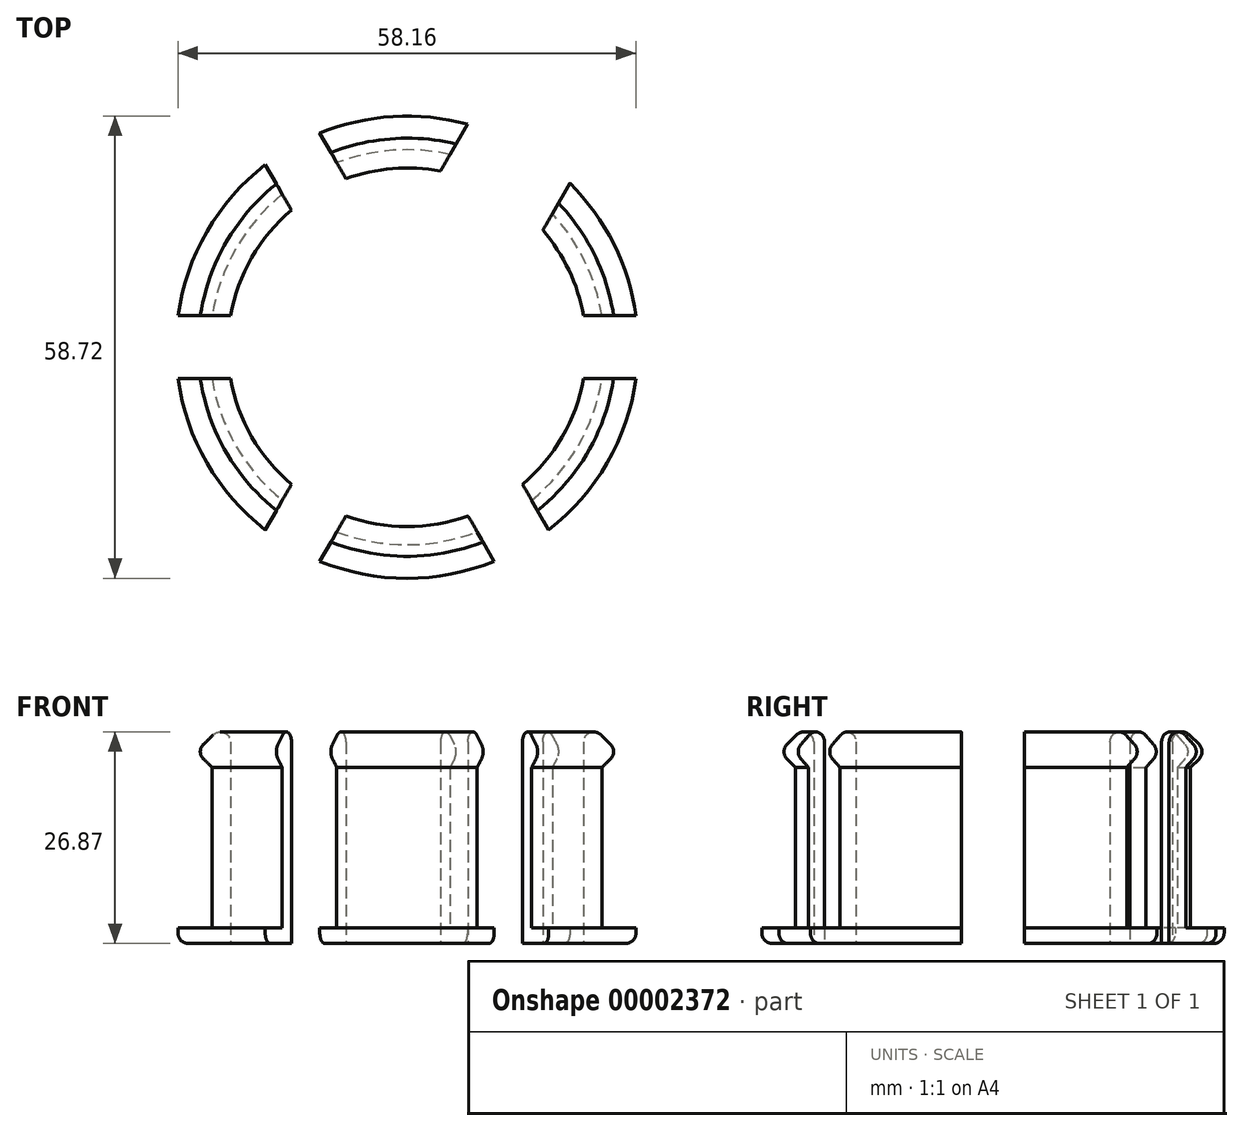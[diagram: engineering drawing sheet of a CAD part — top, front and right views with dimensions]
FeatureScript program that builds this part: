
annotation { "Feature Type Name" : "Feature", "Feature Type Description" : "" }
export const myFeature = defineFeature(function(context is Context, id is Id, definition is map)
    precondition{}
    {
        {
            var Q0;
            Q0=qCreatedBy(makeId("Top.planeOp"),FACE);
            var sketch = newSketch(context, id + "F0", { "sketchPlane" : qUnion([Q0])});
            skArc(sketch, "E0", {"start": v(25.08, 4) * mm, "mid": v(22.84, 11.11) * mm, "end": v(18.63, 17.27) * mm});
            skArc(sketch, "E1.0", {"start": v(29.08, 4) * mm, "mid": v(26.27, 13.1) * mm, "end": v(20.69, 20.83) * mm});
            skLineSegment(sketch, "E2.bottom", {"start": v(21.4, -4) * mm, "end": v(29.08, -4) * mm});
            skLineSegment(sketch, "E2.top", {"start": v(21.4, 4) * mm, "end": v(29.08, 4) * mm});
            skArc(sketch, "E3", {"start": v(21.4, 4) * mm, "mid": v(17.4, 0) * mm, "end": v(21.4, -4) * mm});
            skArc(sketch, "E4.0", {"start": v(22.77, 4) * mm, "mid": v(20.87, 9.96) * mm, "end": v(17.43, 15.2) * mm});
            skLineSegment(sketch, "E5.1.0", {"start": v(7.24, -20.53) * mm, "end": v(11.08, -27.19) * mm});
            skLineSegment(sketch, "E5.1.1", {"start": v(14.16, -16.53) * mm, "end": v(18, -23.19) * mm});
            skArc(sketch, "E5.1.2", {"start": v(14.16, -16.53) * mm, "mid": v(8.7, -15.07) * mm, "end": v(7.24, -20.53) * mm});
            skLineSegment(sketch, "E5.2.0", {"start": v(-14.16, -16.53) * mm, "end": v(-18, -23.19) * mm});
            skLineSegment(sketch, "E5.2.1", {"start": v(-7.24, -20.53) * mm, "end": v(-11.08, -27.19) * mm});
            skArc(sketch, "E5.2.2", {"start": v(-7.24, -20.53) * mm, "mid": v(-8.7, -15.07) * mm, "end": v(-14.16, -16.53) * mm});
            skLineSegment(sketch, "E5.3.0", {"start": v(-21.4, 4) * mm, "end": v(-29.08, 4) * mm});
            skLineSegment(sketch, "E5.3.1", {"start": v(-21.4, -4) * mm, "end": v(-29.08, -4) * mm});
            skArc(sketch, "E5.3.2", {"start": v(-21.4, -4) * mm, "mid": v(-17.4, 0) * mm, "end": v(-21.4, 4) * mm});
            skLineSegment(sketch, "E5.4.0", {"start": v(-7.24, 20.53) * mm, "end": v(-11.08, 27.19) * mm});
            skLineSegment(sketch, "E5.4.1", {"start": v(-14.16, 16.53) * mm, "end": v(-18, 23.19) * mm});
            skArc(sketch, "E5.4.2", {"start": v(-14.16, 16.53) * mm, "mid": v(-8.7, 15.07) * mm, "end": v(-7.24, 20.53) * mm});
            skLineSegment(sketch, "E5.anchor1", {"start": v(0, 0) * mm, "end": v(21.4, 0) * mm, "construction": true});
            skLineSegment(sketch, "E5.anchor2", {"start": v(0, 0) * mm, "end": v(-10.7, 18.53) * mm, "construction": true});
            skArc(sketch, "E6.trimOffspring", {"start": v(-14.85, 17.72) * mm, "mid": v(-20.02, 11.56) * mm, "end": v(-22.77, 4) * mm});
            skArc(sketch, "E7.trimOffspring", {"start": v(-16, 19.72) * mm, "mid": v(-22, 12.7) * mm, "end": v(-25.08, 4) * mm});
            skArc(sketch, "E8.trimOffspring", {"start": v(-18, 23.19) * mm, "mid": v(-25.42, 14.68) * mm, "end": v(-29.08, 4) * mm});
            skArc(sketch, "E9.trimOffspring", {"start": v(-29.08, -4) * mm, "mid": v(-25.42, -14.68) * mm, "end": v(-18, -23.19) * mm});
            skArc(sketch, "E10.trimOffspring", {"start": v(-25.08, -4) * mm, "mid": v(-22, -12.7) * mm, "end": v(-16, -19.72) * mm});
            skArc(sketch, "E11.trimOffspring", {"start": v(-22.77, -4) * mm, "mid": v(-20.02, -11.56) * mm, "end": v(-14.85, -17.72) * mm});
            skArc(sketch, "E12.trimOffspring", {"start": v(-7.92, -21.72) * mm, "mid": v(0, -23.12) * mm, "end": v(7.92, -21.72) * mm});
            skArc(sketch, "E13.trimOffspring", {"start": v(-9.08, -23.72) * mm, "mid": v(0, -25.4) * mm, "end": v(9.08, -23.72) * mm});
            skArc(sketch, "E14.trimOffspring", {"start": v(-11.08, -27.19) * mm, "mid": v(0, -29.36) * mm, "end": v(11.08, -27.19) * mm});
            skArc(sketch, "E15.trimOffspring", {"start": v(14.85, -17.72) * mm, "mid": v(20.02, -11.56) * mm, "end": v(22.77, -4) * mm});
            skArc(sketch, "E16.trimOffspring", {"start": v(16, -19.72) * mm, "mid": v(22, -12.7) * mm, "end": v(25.08, -4) * mm});
            skArc(sketch, "E17.trimOffspring", {"start": v(18, -23.19) * mm, "mid": v(25.42, -14.68) * mm, "end": v(29.08, -4) * mm});
            skLineSegment(sketch, "E18.1.0", {"start": v(15.45, 11.75) * mm, "end": v(20.69, 20.83) * mm});
            skLineSegment(sketch, "E18.1.1", {"start": v(2.45, 19.25) * mm, "end": v(7.7, 28.33) * mm});
            skArc(sketch, "E18.1.2", {"start": v(2.45, 19.25) * mm, "mid": v(5.2, 9) * mm, "end": v(15.45, 11.75) * mm});
            skLineSegment(sketch, "E18.anchor2", {"start": v(0, 0) * mm, "end": v(8.95, 15.5) * mm, "construction": true});
            skArc(sketch, "E19.trimOffspring", {"start": v(4.44, 22.7) * mm, "mid": v(-1.8, 23.05) * mm, "end": v(-7.92, 21.72) * mm});
            skArc(sketch, "E20.trimOffspring", {"start": v(5.64, 24.77) * mm, "mid": v(-1.8, 25.34) * mm, "end": v(-9.08, 23.72) * mm});
            skArc(sketch, "E21.trimOffspring", {"start": v(7.7, 28.33) * mm, "mid": v(-1.78, 29.3) * mm, "end": v(-11.08, 27.19) * mm});
            skLineSegment(sketch, "E22", {"start": v(-14.16, -16.53) * mm, "end": v(-16, -19.72) * mm});
            skLineSegment(sketch, "E23", {"start": v(4.44, 22.7) * mm, "end": v(5.64, 24.77) * mm});
            skLineSegment(sketch, "E24", {"start": v(-14.85, 17.72) * mm, "end": v(-18, 23.19) * mm});
            skLineSegment(sketch, "E25", {"start": v(-11.08, 27.19) * mm, "end": v(-7.92, 21.72) * mm});
            skLineSegment(sketch, "E26", {"start": v(7.7, 28.33) * mm, "end": v(4.44, 22.7) * mm});
            skLineSegment(sketch, "E27", {"start": v(20.69, 20.83) * mm, "end": v(17.43, 15.2) * mm});
            skLineSegment(sketch, "E28", {"start": v(29.08, 4) * mm, "end": v(22.77, 4) * mm});
            skLineSegment(sketch, "E29", {"start": v(29.08, -4) * mm, "end": v(22.77, -4) * mm});
            skLineSegment(sketch, "E30", {"start": v(18, -23.19) * mm, "end": v(14.85, -17.72) * mm});
            skLineSegment(sketch, "E31", {"start": v(-11.08, -27.19) * mm, "end": v(-7.92, -21.72) * mm});
            skLineSegment(sketch, "E32", {"start": v(-18, -23.19) * mm, "end": v(-14.85, -17.72) * mm});
            skLineSegment(sketch, "E33", {"start": v(-29.08, -4) * mm, "end": v(-22.77, -4) * mm});
            skLineSegment(sketch, "E34", {"start": v(-29.08, 4) * mm, "end": v(-22.77, 4) * mm});
            skLineSegment(sketch, "E35", {"start": v(7.92, -21.72) * mm, "end": v(11.08, -27.19) * mm});
            skLineSegment(sketch, "E36", {"start": v(29.08, -4) * mm, "end": v(29.08, 4) * mm});
            skLineSegment(sketch, "E37", {"start": v(-18, 23.19) * mm, "end": v(-11.08, 27.19) * mm});
            skLineSegment(sketch, "E38", {"start": v(-29.08, -4) * mm, "end": v(-29.08, 4) * mm});
            skLineSegment(sketch, "E39", {"start": v(-18, -23.19) * mm, "end": v(-11.08, -27.19) * mm});
            skLineSegment(sketch, "E40", {"start": v(11.08, -27.19) * mm, "end": v(18, -23.19) * mm});
            skLineSegment(sketch, "E41", {"start": v(7.7, 28.33) * mm, "end": v(20.69, 20.83) * mm});
            skSolve(sketch);
        }
        {
            var Q0;
            {var subQ2=sQuery(id+"F0.wireOp",EDGE,"E0");Q0=makeQuery(id+"F0.imprint","IMPRINT",FACE,{"disambiguationData":[TD([[makeQuery(id+"F0.imprint","IMPRINT",EDGE,{"derivedFrom":subQ2}),-1.0]])]});}
            var Q1;
            {var subQ2=sQuery(id+"F0.wireOp",EDGE,"E7.trimOffspring");Q1=makeQuery(id+"F0.imprint","IMPRINT",FACE,{"disambiguationData":[TD([[makeQuery(id+"F0.imprint","IMPRINT",EDGE,{"derivedFrom":subQ2}),-1.0]])]});}
            var Q2;
            {var subQ2=sQuery(id+"F0.wireOp",EDGE,"E9.trimOffspring");Q2=makeQuery(id+"F0.imprint","IMPRINT",FACE,{"disambiguationData":[TD([[makeQuery(id+"F0.imprint","IMPRINT",EDGE,{"derivedFrom":subQ2}),1.0]])]});}
            var Q3;
            {var subQ2=sQuery(id+"F0.wireOp",EDGE,"E13.trimOffspring");Q3=makeQuery(id+"F0.imprint","IMPRINT",FACE,{"disambiguationData":[TD([[makeQuery(id+"F0.imprint","IMPRINT",EDGE,{"derivedFrom":subQ2}),-1.0]])]});}
            var Q4;
            {var subQ2=sQuery(id+"F0.wireOp",EDGE,"E16.trimOffspring");Q4=makeQuery(id+"F0.imprint","IMPRINT",FACE,{"disambiguationData":[TD([[makeQuery(id+"F0.imprint","IMPRINT",EDGE,{"derivedFrom":subQ2}),-1.0]])]});}
            var Q5;
            {var subQ2=sQuery(id+"F0.wireOp",EDGE,"E20.trimOffspring");Q5=makeQuery(id+"F0.imprint","IMPRINT",FACE,{"disambiguationData":[TD([[makeQuery(id+"F0.imprint","IMPRINT",EDGE,{"derivedFrom":subQ2}),-1.0]])]});}
            var Q6;
            {var subQ2=sQuery(id+"F0.wireOp",EDGE,"E18.1.0");Q6=makeQuery(id+"F0.imprint","IMPRINT",FACE,{"disambiguationData":[TD([[makeQuery(id+"F0.imprint","IMPRINT",EDGE,{"derivedFrom":subQ2}),1.0]])]});}
            var Q7;
            {var subQ2=sQuery(id+"F0.wireOp",EDGE,"E12.trimOffspring");Q7=makeQuery(id+"F0.imprint","IMPRINT",FACE,{"disambiguationData":[TD([[makeQuery(id+"F0.imprint","IMPRINT",EDGE,{"derivedFrom":subQ2}),-1.0]])]});}
            var Q8;
            {var subQ2=sQuery(id+"F0.wireOp",EDGE,"E10.trimOffspring");Q8=makeQuery(id+"F0.imprint","IMPRINT",FACE,{"disambiguationData":[TD([[makeQuery(id+"F0.imprint","IMPRINT",EDGE,{"derivedFrom":subQ2}),1.0]])]});}
            var Q9;
            {var subQ2=sQuery(id+"F0.wireOp",EDGE,"E6.trimOffspring");Q9=makeQuery(id+"F0.imprint","IMPRINT",FACE,{"disambiguationData":[TD([[makeQuery(id+"F0.imprint","IMPRINT",EDGE,{"derivedFrom":subQ2}),-1.0]])]});}
            var Q10;
            Q10=makeQuery(id+"F0.imprint","IMPRINT",FACE,{"disambiguationData":[TD([[makeQuery(id+"F0.imprint","IMPRINT",EDGE,{"derivedFrom":sQuery(id+"F0.wireOp",EDGE,"E2.bottom")}),-1.0]])]});
            var Q11;
            {var subQ2=sQuery(id+"F0.wireOp",EDGE,"E15.trimOffspring");Q11=makeQuery(id+"F0.imprint","IMPRINT",FACE,{"disambiguationData":[TD([[makeQuery(id+"F0.imprint","IMPRINT",EDGE,{"derivedFrom":subQ2}),-1.0]])]});}
            var Q12;
            {var subQ2=sQuery(id+"F0.wireOp",EDGE,"E0");Q12=makeQuery(id+"F0.imprint","IMPRINT",FACE,{"disambiguationData":[TD([[makeQuery(id+"F0.imprint","IMPRINT",EDGE,{"derivedFrom":subQ2}),1.0]])]});}
            var Q13;
            {var subQ2=sQuery(id+"F0.wireOp",EDGE,"E19.trimOffspring");Q13=makeQuery(id+"F0.imprint","IMPRINT",FACE,{"disambiguationData":[TD([[makeQuery(id+"F0.imprint","IMPRINT",EDGE,{"derivedFrom":subQ2}),-1.0]])]});}
            var Q14;
            {var subQ3=sQuery(id+"F0.wireOp",EDGE,"E2.bottom");Q14=makeQuery(id+"F0.imprint","IMPRINT",FACE,{"disambiguationData":[TD([[makeQuery(id+"F0.imprint","IMPRINT",EDGE,{"derivedFrom":subQ3}),1.0]])]});}
            var Q15;
            {var subQ6=sQuery(id+"F0.wireOp",EDGE,"E5.1.0");Q15=makeQuery(id+"F0.imprint","IMPRINT",FACE,{"disambiguationData":[TD([[makeQuery(id+"F0.imprint","IMPRINT",EDGE,{"derivedFrom":subQ6}),1.0]])]});}
            var Q16;
            {var subQ6=sQuery(id+"F0.wireOp",EDGE,"E5.2.1");Q16=makeQuery(id+"F0.imprint","IMPRINT",FACE,{"disambiguationData":[TD([[makeQuery(id+"F0.imprint","IMPRINT",EDGE,{"derivedFrom":subQ6}),-1.0]])]});}
            var Q17;
            {var subQ2=sQuery(id+"F0.wireOp",EDGE,"E5.3.0");Q17=makeQuery(id+"F0.imprint","IMPRINT",FACE,{"disambiguationData":[TD([[makeQuery(id+"F0.imprint","IMPRINT",EDGE,{"derivedFrom":subQ2}),1.0]])]});}
            var Q18;
            {var subQ3=sQuery(id+"F0.wireOp",EDGE,"E5.4.0");Q18=makeQuery(id+"F0.imprint","IMPRINT",FACE,{"disambiguationData":[TD([[makeQuery(id+"F0.imprint","IMPRINT",EDGE,{"derivedFrom":subQ3}),1.0]])]});}
            extrude(context, id + "F1", {"entities" : qUnion([Q0, Q1, Q2, Q3, Q4, Q5, Q6, Q7, Q8, Q9, Q10, Q11, Q12, Q13, Q14, Q15, Q16, Q17, Q18]), "depth" : 2 * mm});
        }
        {
            var Q0;
            Q0=qCreatedBy(makeId("Front.planeOp"),FACE);
            var sketch = newSketch(context, id + "F2", { "sketchPlane" : qUnion([Q0])});
            skLineSegment(sketch, "E42", {"start": v(27.08, 24.35) * mm, "end": v(25.08, 22.35) * mm});
            skLineSegment(sketch, "E43", {"start": v(25.08, 22.35) * mm, "end": v(25.08, 26.35) * mm, "construction": true});
            skLineSegment(sketch, "E44", {"start": v(25.08, 24.35) * mm, "end": v(27.08, 24.35) * mm, "construction": true});
            skLineSegment(sketch, "E45", {"start": v(22.77, 28.66) * mm, "end": v(25.08, 26.35) * mm});
            skLineSegment(sketch, "E46", {"start": v(25.08, 26.35) * mm, "end": v(27.08, 24.35) * mm});
            skPoint(sketch, "E47.0", {"position": v(25.08, 0) * mm});
            skPoint(sketch, "E47.1", {"position": v(22.77, 0) * mm});
            skLineSegment(sketch, "E48", {"start": v(25.08, 22.35) * mm, "end": v(25.08, 0) * mm});
            skLineSegment(sketch, "E49", {"start": v(22.77, 0) * mm, "end": v(22.77, 28.66) * mm});
            skLineSegment(sketch, "E50", {"start": v(25.08, 0) * mm, "end": v(22.77, 0) * mm});
            skLineSegment(sketch, "E51", {"start": v(0, 0) * mm, "end": v(0, 28.66) * mm});
            skSolve(sketch);
        }
        {
            var Q0;
            Q0=makeQuery(id+"F2.imprint","IMPRINT",FACE,{"disambiguationData":[TD([[makeQuery(id+"F2.imprint","IMPRINT",EDGE,{"derivedFrom":sQuery(id+"F2.wireOp",EDGE,"E42")}),-1.0]])]});
            var Q1;
            Q1=sQuery(id+"F2.wireOp",EDGE,"E42");
            var Q2;
            Q2=sQuery(id+"F2.wireOp",EDGE,"E46");
            var Q3;
            Q3=sQuery(id+"F2.wireOp",EDGE,"E45");
            var Q4;
            Q4=sQuery(id+"F2.wireOp",EDGE,"E49");
            var Q5;
            Q5=sQuery(id+"F2.wireOp",EDGE,"E48");
            var Q6;
            Q6=sQuery(id+"F2.wireOp",EDGE,"E51");
            revolve(context, id + "F3", {"operationType" : NewBodyOperationType.ADD, "entities" : qUnion([Q0]), "surfaceEntities" : qUnion([Q1, Q2, Q3, Q4, Q5]), "axis" : qUnion([Q6]), "revolveType" : RevolveType.FULL});
        }
        {
            var Q0;
            {var subQ6=sQuery(id+"F0.wireOp",EDGE,"E5.2.1");Q0=makeQuery(id+"F0.imprint","IMPRINT",FACE,{"disambiguationData":[TD([[makeQuery(id+"F0.imprint","IMPRINT",EDGE,{"derivedFrom":subQ6}),-1.0]])]});}
            var Q1;
            {var subQ6=sQuery(id+"F0.wireOp",EDGE,"E5.1.0");Q1=makeQuery(id+"F0.imprint","IMPRINT",FACE,{"disambiguationData":[TD([[makeQuery(id+"F0.imprint","IMPRINT",EDGE,{"derivedFrom":subQ6}),1.0]])]});}
            var Q2;
            {var subQ3=sQuery(id+"F0.wireOp",EDGE,"E2.bottom");Q2=makeQuery(id+"F0.imprint","IMPRINT",FACE,{"disambiguationData":[TD([[makeQuery(id+"F0.imprint","IMPRINT",EDGE,{"derivedFrom":subQ3}),1.0]])]});}
            var Q3;
            {var subQ2=sQuery(id+"F0.wireOp",EDGE,"E18.1.0");Q3=makeQuery(id+"F0.imprint","IMPRINT",FACE,{"disambiguationData":[TD([[makeQuery(id+"F0.imprint","IMPRINT",EDGE,{"derivedFrom":subQ2}),1.0]])]});}
            var Q4;
            {var subQ3=sQuery(id+"F0.wireOp",EDGE,"E5.4.0");Q4=makeQuery(id+"F0.imprint","IMPRINT",FACE,{"disambiguationData":[TD([[makeQuery(id+"F0.imprint","IMPRINT",EDGE,{"derivedFrom":subQ3}),1.0]])]});}
            var Q5;
            {var subQ2=sQuery(id+"F0.wireOp",EDGE,"E5.3.0");Q5=makeQuery(id+"F0.imprint","IMPRINT",FACE,{"disambiguationData":[TD([[makeQuery(id+"F0.imprint","IMPRINT",EDGE,{"derivedFrom":subQ2}),1.0]])]});}
            extrude(context, id + "F4", {"entities" : qUnion([Q0, Q1, Q2, Q3, Q4, Q5]), "operationType" : NewBodyOperationType.REMOVE, "endBound" : BoundingType.THROUGH_ALL, "depth" : 31.75 * mm});
        }
        {
            var Q0;
            Q0=makeQuery(id+"F4.boolean.opBoolean","COPY",EDGE,{"derivedFrom":makeQuery(id+"F4.opExtrude","CAP_EDGE",EDGE,{"disambiguationData":[OSD([sQuery(id+"F0.wireOp",EDGE,"E5.2.2")])],"isStart":true})});
            var Q1;
            Q1=makeQuery(id+"F4.boolean.opBoolean","COPY",EDGE,{"derivedFrom":makeQuery(id+"F4.opExtrude","CAP_EDGE",EDGE,{"disambiguationData":[OSD([sQuery(id+"F0.wireOp",EDGE,"E5.1.2")])],"isStart":true})});
            var Q2;
            Q2=makeQuery(id+"F4.boolean.opBoolean","COPY",EDGE,{"derivedFrom":makeQuery(id+"F4.opExtrude","CAP_EDGE",EDGE,{"disambiguationData":[OSD([sQuery(id+"F0.wireOp",EDGE,"E3")])],"isStart":true})});
            var Q3;
            Q3=makeQuery(id+"F4.boolean.opBoolean","COPY",EDGE,{"derivedFrom":makeQuery(id+"F4.opExtrude","CAP_EDGE",EDGE,{"disambiguationData":[OSD([sQuery(id+"F0.wireOp",EDGE,"E18.1.2")])],"isStart":true})});
            var Q4;
            Q4=makeQuery(id+"F4.boolean.opBoolean","COPY",EDGE,{"derivedFrom":makeQuery(id+"F4.opExtrude","CAP_EDGE",EDGE,{"disambiguationData":[OSD([sQuery(id+"F0.wireOp",EDGE,"E5.4.2")])],"isStart":true})});
            var Q5;
            Q5=makeQuery(id+"F4.boolean.opBoolean","COPY",EDGE,{"derivedFrom":makeQuery(id+"F4.opExtrude","CAP_EDGE",EDGE,{"disambiguationData":[OSD([sQuery(id+"F0.wireOp",EDGE,"E5.3.2")])],"isStart":true})});
            var Q6;
            Q6=makeQuery(id+"F1.opExtrude","CAP_EDGE",EDGE,{"disambiguationData":[OSD([sQuery(id+"F0.wireOp",EDGE,"E21.trimOffspring")])],"isStart":true});
            var Q7;
            Q7=makeQuery(id+"F1.opExtrude","CAP_EDGE",EDGE,{"disambiguationData":[OSD([sQuery(id+"F0.wireOp",EDGE,"E8.trimOffspring")])],"isStart":true});
            var Q8;
            Q8=makeQuery(id+"F1.opExtrude","CAP_EDGE",EDGE,{"disambiguationData":[OSD([sQuery(id+"F0.wireOp",EDGE,"E9.trimOffspring")])],"isStart":true});
            var Q9;
            Q9=makeQuery(id+"F1.opExtrude","CAP_EDGE",EDGE,{"disambiguationData":[OSD([sQuery(id+"F0.wireOp",EDGE,"E14.trimOffspring")])],"isStart":true});
            var Q10;
            Q10=makeQuery(id+"F1.opExtrude","CAP_EDGE",EDGE,{"disambiguationData":[OSD([sQuery(id+"F0.wireOp",EDGE,"E17.trimOffspring")])],"isStart":true});
            var Q11;
            Q11=makeQuery(id+"F1.opExtrude","CAP_EDGE",EDGE,{"disambiguationData":[OSD([sQuery(id+"F0.wireOp",EDGE,"E1.0")])],"isStart":true});
            var Q12;
            {var subQ0=makeQuery(id+"F1.opExtrude","CAP_FACE",FACE,{"disambiguationData":[OSD([sQuery(id+"F0.wireOp",EDGE,"E1.0"),sQuery(id+"F0.wireOp",EDGE,"E8.trimOffspring"),sQuery(id+"F0.wireOp",EDGE,"E9.trimOffspring"),sQuery(id+"F0.wireOp",EDGE,"E14.trimOffspring"),sQuery(id+"F0.wireOp",EDGE,"E17.trimOffspring"),sQuery(id+"F0.wireOp",EDGE,"E21.trimOffspring"),sQuery(id+"F0.wireOp",EDGE,"E36"),sQuery(id+"F0.wireOp",EDGE,"E37"),sQuery(id+"F0.wireOp",EDGE,"E38"),sQuery(id+"F0.wireOp",EDGE,"E39"),sQuery(id+"F0.wireOp",EDGE,"E40"),sQuery(id+"F0.wireOp",EDGE,"E41")])],"isStart":false});var subQ1=makeQuery(id+"F3.opRevolve","SWEPT_FACE",FACE,{"disambiguationData":[OSD([sQuery(id+"F2.wireOp",EDGE,"E49")])]});Q12=makeQuery(id+"F4.boolean.opBoolean","SPLIT",EDGE,{"disambiguationData":[TD([makeQuery(id+"F4.opExtrude","SWEPT_FACE",FACE,{"disambiguationData":[OSD([sQuery(id+"F0.wireOp",EDGE,"E5.4.0"),sQuery(id+"F0.wireOp",EDGE,"E25")])]})])],"derivedFrom":makeQuery(id+"F3.boolean.opBoolean","INTERSECT",EDGE,{"derivedFrom":[subQ0,subQ1]})});}
            var Q13;
            {var subQ0=makeQuery(id+"F1.opExtrude","CAP_FACE",FACE,{"disambiguationData":[OSD([sQuery(id+"F0.wireOp",EDGE,"E1.0"),sQuery(id+"F0.wireOp",EDGE,"E8.trimOffspring"),sQuery(id+"F0.wireOp",EDGE,"E9.trimOffspring"),sQuery(id+"F0.wireOp",EDGE,"E14.trimOffspring"),sQuery(id+"F0.wireOp",EDGE,"E17.trimOffspring"),sQuery(id+"F0.wireOp",EDGE,"E21.trimOffspring"),sQuery(id+"F0.wireOp",EDGE,"E36"),sQuery(id+"F0.wireOp",EDGE,"E37"),sQuery(id+"F0.wireOp",EDGE,"E38"),sQuery(id+"F0.wireOp",EDGE,"E39"),sQuery(id+"F0.wireOp",EDGE,"E40"),sQuery(id+"F0.wireOp",EDGE,"E41")])],"isStart":false});var subQ1=makeQuery(id+"F3.opRevolve","SWEPT_FACE",FACE,{"disambiguationData":[OSD([sQuery(id+"F2.wireOp",EDGE,"E49")])]});Q13=makeQuery(id+"F4.boolean.opBoolean","SPLIT",EDGE,{"disambiguationData":[TD([makeQuery(id+"F4.opExtrude","SWEPT_FACE",FACE,{"disambiguationData":[OSD([sQuery(id+"F0.wireOp",EDGE,"E5.3.0"),sQuery(id+"F0.wireOp",EDGE,"E34")])]})])],"derivedFrom":makeQuery(id+"F3.boolean.opBoolean","INTERSECT",EDGE,{"derivedFrom":[subQ0,subQ1]})});}
            var Q14;
            {var subQ0=makeQuery(id+"F1.opExtrude","CAP_FACE",FACE,{"disambiguationData":[OSD([sQuery(id+"F0.wireOp",EDGE,"E1.0"),sQuery(id+"F0.wireOp",EDGE,"E8.trimOffspring"),sQuery(id+"F0.wireOp",EDGE,"E9.trimOffspring"),sQuery(id+"F0.wireOp",EDGE,"E14.trimOffspring"),sQuery(id+"F0.wireOp",EDGE,"E17.trimOffspring"),sQuery(id+"F0.wireOp",EDGE,"E21.trimOffspring"),sQuery(id+"F0.wireOp",EDGE,"E36"),sQuery(id+"F0.wireOp",EDGE,"E37"),sQuery(id+"F0.wireOp",EDGE,"E38"),sQuery(id+"F0.wireOp",EDGE,"E39"),sQuery(id+"F0.wireOp",EDGE,"E40"),sQuery(id+"F0.wireOp",EDGE,"E41")])],"isStart":false});var subQ1=makeQuery(id+"F3.opRevolve","SWEPT_FACE",FACE,{"disambiguationData":[OSD([sQuery(id+"F2.wireOp",EDGE,"E49")])]});Q14=makeQuery(id+"F4.boolean.opBoolean","SPLIT",EDGE,{"disambiguationData":[TD([makeQuery(id+"F4.opExtrude","SWEPT_FACE",FACE,{"disambiguationData":[OSD([sQuery(id+"F0.wireOp",EDGE,"E5.3.1"),sQuery(id+"F0.wireOp",EDGE,"E33")])]})])],"derivedFrom":makeQuery(id+"F3.boolean.opBoolean","INTERSECT",EDGE,{"derivedFrom":[subQ0,subQ1]})});}
            var Q15;
            {var subQ0=makeQuery(id+"F1.opExtrude","CAP_FACE",FACE,{"disambiguationData":[OSD([sQuery(id+"F0.wireOp",EDGE,"E1.0"),sQuery(id+"F0.wireOp",EDGE,"E8.trimOffspring"),sQuery(id+"F0.wireOp",EDGE,"E9.trimOffspring"),sQuery(id+"F0.wireOp",EDGE,"E14.trimOffspring"),sQuery(id+"F0.wireOp",EDGE,"E17.trimOffspring"),sQuery(id+"F0.wireOp",EDGE,"E21.trimOffspring"),sQuery(id+"F0.wireOp",EDGE,"E36"),sQuery(id+"F0.wireOp",EDGE,"E37"),sQuery(id+"F0.wireOp",EDGE,"E38"),sQuery(id+"F0.wireOp",EDGE,"E39"),sQuery(id+"F0.wireOp",EDGE,"E40"),sQuery(id+"F0.wireOp",EDGE,"E41")])],"isStart":false});var subQ1=makeQuery(id+"F3.opRevolve","SWEPT_FACE",FACE,{"disambiguationData":[OSD([sQuery(id+"F2.wireOp",EDGE,"E49")])]});Q15=makeQuery(id+"F4.boolean.opBoolean","SPLIT",EDGE,{"disambiguationData":[TD([makeQuery(id+"F4.opExtrude","SWEPT_FACE",FACE,{"disambiguationData":[OSD([sQuery(id+"F0.wireOp",EDGE,"E5.1.0"),sQuery(id+"F0.wireOp",EDGE,"E35")])]})])],"derivedFrom":makeQuery(id+"F3.boolean.opBoolean","INTERSECT",EDGE,{"derivedFrom":[subQ0,subQ1]})});}
            var Q16;
            {var subQ0=makeQuery(id+"F1.opExtrude","CAP_FACE",FACE,{"disambiguationData":[OSD([sQuery(id+"F0.wireOp",EDGE,"E1.0"),sQuery(id+"F0.wireOp",EDGE,"E8.trimOffspring"),sQuery(id+"F0.wireOp",EDGE,"E9.trimOffspring"),sQuery(id+"F0.wireOp",EDGE,"E14.trimOffspring"),sQuery(id+"F0.wireOp",EDGE,"E17.trimOffspring"),sQuery(id+"F0.wireOp",EDGE,"E21.trimOffspring"),sQuery(id+"F0.wireOp",EDGE,"E36"),sQuery(id+"F0.wireOp",EDGE,"E37"),sQuery(id+"F0.wireOp",EDGE,"E38"),sQuery(id+"F0.wireOp",EDGE,"E39"),sQuery(id+"F0.wireOp",EDGE,"E40"),sQuery(id+"F0.wireOp",EDGE,"E41")])],"isStart":false});var subQ1=makeQuery(id+"F3.opRevolve","SWEPT_FACE",FACE,{"disambiguationData":[OSD([sQuery(id+"F2.wireOp",EDGE,"E49")])]});Q16=makeQuery(id+"F4.boolean.opBoolean","SPLIT",EDGE,{"disambiguationData":[TD([makeQuery(id+"F4.opExtrude","SWEPT_FACE",FACE,{"disambiguationData":[OSD([sQuery(id+"F0.wireOp",EDGE,"E2.bottom"),sQuery(id+"F0.wireOp",EDGE,"E29")])]})])],"derivedFrom":makeQuery(id+"F3.boolean.opBoolean","INTERSECT",EDGE,{"derivedFrom":[subQ0,subQ1]})});}
            var Q17;
            {var subQ0=makeQuery(id+"F1.opExtrude","CAP_FACE",FACE,{"disambiguationData":[OSD([sQuery(id+"F0.wireOp",EDGE,"E1.0"),sQuery(id+"F0.wireOp",EDGE,"E8.trimOffspring"),sQuery(id+"F0.wireOp",EDGE,"E9.trimOffspring"),sQuery(id+"F0.wireOp",EDGE,"E14.trimOffspring"),sQuery(id+"F0.wireOp",EDGE,"E17.trimOffspring"),sQuery(id+"F0.wireOp",EDGE,"E21.trimOffspring"),sQuery(id+"F0.wireOp",EDGE,"E36"),sQuery(id+"F0.wireOp",EDGE,"E37"),sQuery(id+"F0.wireOp",EDGE,"E38"),sQuery(id+"F0.wireOp",EDGE,"E39"),sQuery(id+"F0.wireOp",EDGE,"E40"),sQuery(id+"F0.wireOp",EDGE,"E41")])],"isStart":false});var subQ1=makeQuery(id+"F3.opRevolve","SWEPT_FACE",FACE,{"disambiguationData":[OSD([sQuery(id+"F2.wireOp",EDGE,"E49")])]});Q17=makeQuery(id+"F4.boolean.opBoolean","SPLIT",EDGE,{"disambiguationData":[TD([makeQuery(id+"F4.opExtrude","SWEPT_FACE",FACE,{"disambiguationData":[OSD([sQuery(id+"F0.wireOp",EDGE,"E2.top"),sQuery(id+"F0.wireOp",EDGE,"E28")])]})])],"derivedFrom":makeQuery(id+"F3.boolean.opBoolean","INTERSECT",EDGE,{"derivedFrom":[subQ0,subQ1]})});}
            var Q18;
            {var subQ0=sQuery(id+"F2.wireOp",EDGE,"E46");var subQ1=sQuery(id+"F2.wireOp",EDGE,"E49");Q18=makeQuery(id+"F4.boolean.opBoolean","SPLIT",EDGE,{"disambiguationData":[TD([makeQuery(id+"F4.opExtrude","SWEPT_FACE",FACE,{"disambiguationData":[OSD([sQuery(id+"F0.wireOp",EDGE,"E5.3.1"),sQuery(id+"F0.wireOp",EDGE,"E33")])]})])],"derivedFrom":makeQuery(id+"F3.opRevolve","SWEPT_EDGE",EDGE,{"disambiguationData":[OSD([subQ0,subQ1])]})});}
            var Q19;
            {var subQ0=sQuery(id+"F2.wireOp",EDGE,"E46");var subQ1=sQuery(id+"F2.wireOp",EDGE,"E49");Q19=makeQuery(id+"F4.boolean.opBoolean","SPLIT",EDGE,{"disambiguationData":[TD([makeQuery(id+"F4.opExtrude","SWEPT_FACE",FACE,{"disambiguationData":[OSD([sQuery(id+"F0.wireOp",EDGE,"E5.3.0"),sQuery(id+"F0.wireOp",EDGE,"E34")])]})])],"derivedFrom":makeQuery(id+"F3.opRevolve","SWEPT_EDGE",EDGE,{"disambiguationData":[OSD([subQ0,subQ1])]})});}
            var Q20;
            {var subQ0=sQuery(id+"F2.wireOp",EDGE,"E46");var subQ1=sQuery(id+"F2.wireOp",EDGE,"E49");Q20=makeQuery(id+"F4.boolean.opBoolean","SPLIT",EDGE,{"disambiguationData":[TD([makeQuery(id+"F4.opExtrude","SWEPT_FACE",FACE,{"disambiguationData":[OSD([sQuery(id+"F0.wireOp",EDGE,"E5.4.0"),sQuery(id+"F0.wireOp",EDGE,"E25")])]})])],"derivedFrom":makeQuery(id+"F3.opRevolve","SWEPT_EDGE",EDGE,{"disambiguationData":[OSD([subQ0,subQ1])]})});}
            var Q21;
            {var subQ0=sQuery(id+"F2.wireOp",EDGE,"E46");var subQ1=sQuery(id+"F2.wireOp",EDGE,"E49");Q21=makeQuery(id+"F4.boolean.opBoolean","SPLIT",EDGE,{"disambiguationData":[TD([makeQuery(id+"F4.opExtrude","SWEPT_FACE",FACE,{"disambiguationData":[OSD([sQuery(id+"F0.wireOp",EDGE,"E2.top"),sQuery(id+"F0.wireOp",EDGE,"E28")])]})])],"derivedFrom":makeQuery(id+"F3.opRevolve","SWEPT_EDGE",EDGE,{"disambiguationData":[OSD([subQ0,subQ1])]})});}
            var Q22;
            {var subQ0=sQuery(id+"F2.wireOp",EDGE,"E46");var subQ1=sQuery(id+"F2.wireOp",EDGE,"E49");Q22=makeQuery(id+"F4.boolean.opBoolean","SPLIT",EDGE,{"disambiguationData":[TD([makeQuery(id+"F4.opExtrude","SWEPT_FACE",FACE,{"disambiguationData":[OSD([sQuery(id+"F0.wireOp",EDGE,"E2.bottom"),sQuery(id+"F0.wireOp",EDGE,"E29")])]})])],"derivedFrom":makeQuery(id+"F3.opRevolve","SWEPT_EDGE",EDGE,{"disambiguationData":[OSD([subQ0,subQ1])]})});}
            var Q23;
            {var subQ0=sQuery(id+"F2.wireOp",EDGE,"E46");var subQ1=sQuery(id+"F2.wireOp",EDGE,"E49");Q23=makeQuery(id+"F4.boolean.opBoolean","SPLIT",EDGE,{"disambiguationData":[TD([makeQuery(id+"F4.opExtrude","SWEPT_FACE",FACE,{"disambiguationData":[OSD([sQuery(id+"F0.wireOp",EDGE,"E5.1.0"),sQuery(id+"F0.wireOp",EDGE,"E35")])]})])],"derivedFrom":makeQuery(id+"F3.opRevolve","SWEPT_EDGE",EDGE,{"disambiguationData":[OSD([subQ0,subQ1])]})});}
            fillet(context, id + "F5", {"entities" : qUnion([Q0, Q1, Q2, Q3, Q4, Q5, Q6, Q7, Q8, Q9, Q10, Q11, Q12, Q13, Q14, Q15, Q16, Q17, Q18, Q19, Q20, Q21, Q22, Q23]), "radius" : 1.27 * mm, "tangentPropagation" : true, "allowEdgeOverflow" : false});
        }
    });
